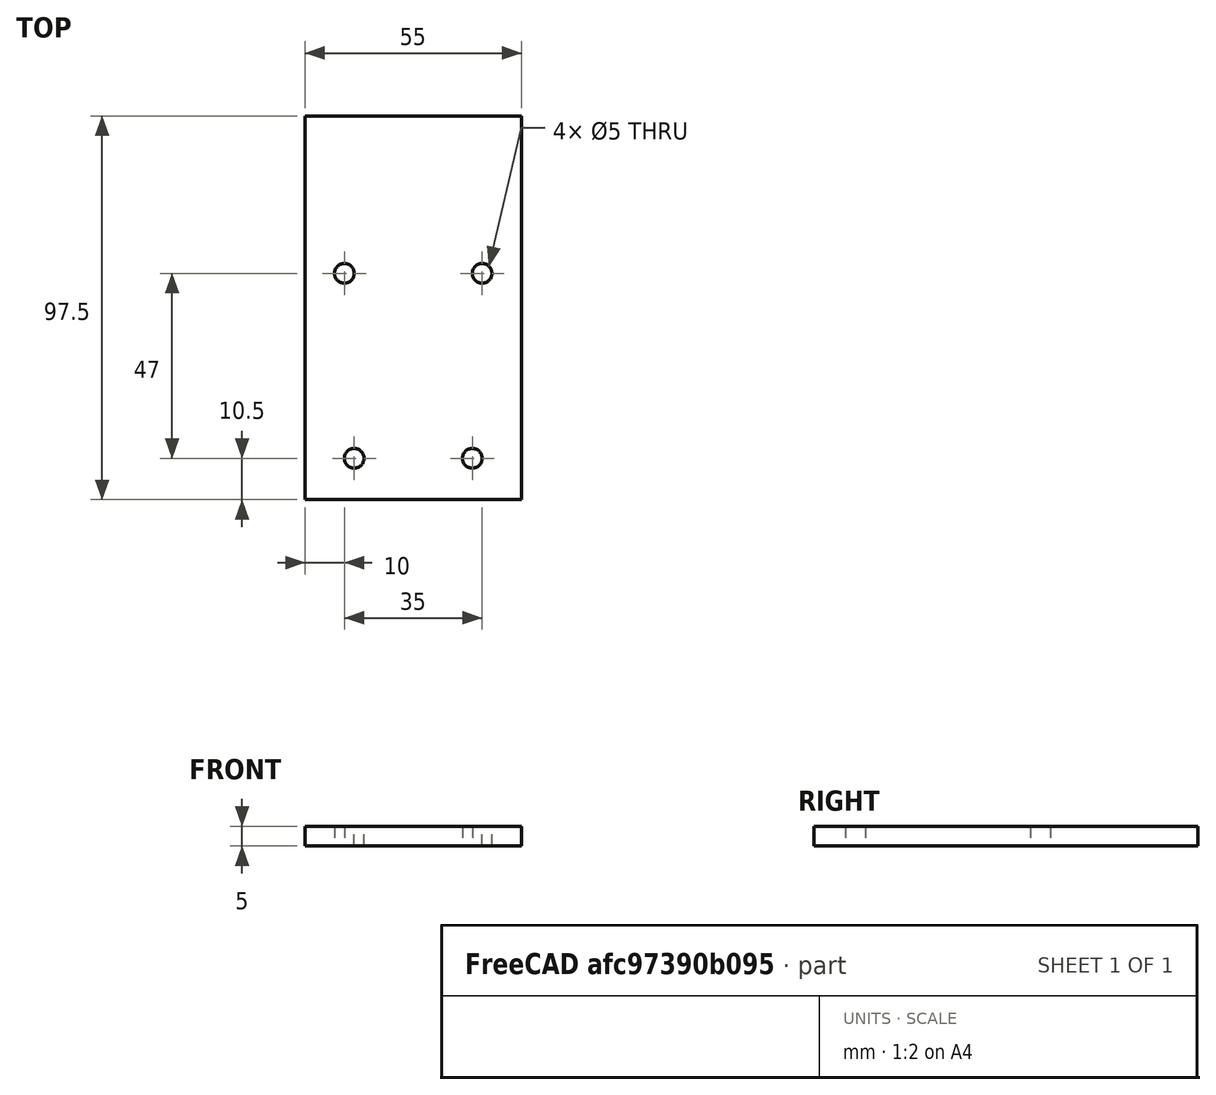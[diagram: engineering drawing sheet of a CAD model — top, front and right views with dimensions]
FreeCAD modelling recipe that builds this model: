
FCSTD DOCUMENT  (FreeCAD 0.18R15115 (Git))
Label: x axis mount plate
License: All rights reserved
LicenseURL: http://en.wikipedia.org/wiki/All_rights_reserved
objects: TechDraw::DrawProjGroupItem×3, TechDraw::DrawProjGroup×3, TechDraw::DrawViewPart×2, Sketcher::SketchObject×1, PartDesign::Pad×1, PartDesign::Body×1, TechDraw::DrawSVGTemplate×1, TechDraw::DrawPage×1
note: 4 computed .brp shape members not serialized (recipe doc carries the construction recipe); baked Part::Feature solids carry a one-line shape summary decoded from their .brp

FEATURE [Sketcher::SketchObject] Sketch
  MapMode = 5
  Support = -> [XY_Plane]
  sketch-geometry (35):
    g0: LineSegment [constr] StartX=0 StartY=0 StartZ=0 EndX=25 EndY=0 EndZ=0
    g1: LineSegment [constr] StartX=25 StartY=0 StartZ=0 EndX=25 EndY=25 EndZ=0
    g2: LineSegment [constr] StartX=25 StartY=25 StartZ=0 EndX=0 EndY=25 EndZ=0
    g3: LineSegment [constr] StartX=0 StartY=25 StartZ=0 EndX=0 EndY=0 EndZ=0
    g4: LineSegment [constr] StartX=-30 StartY=0 StartZ=0 EndX=-5 EndY=0 EndZ=0
    g5: LineSegment [constr] StartX=-5 StartY=0 StartZ=0 EndX=-5 EndY=25 EndZ=0
    g6: LineSegment [constr] StartX=-5 StartY=25 StartZ=0 EndX=-30 EndY=25 EndZ=0
    g7: LineSegment [constr] StartX=-30 StartY=25 StartZ=0 EndX=-30 EndY=0 EndZ=0
    g8: Circle CenterX=12.5 CenterY=35.5 CenterZ=0 NormalX=0 NormalY=0 NormalZ=1 AngleXU=0 Radius=2.5
    g9: Circle CenterX=-17.5 CenterY=35.5 CenterZ=0 NormalX=0 NormalY=0 NormalZ=1 AngleXU=0 Radius=2.5
    g10: LineSegment [constr] StartX=0 StartY=25 StartZ=0 EndX=12.5 EndY=35.5 EndZ=0
    g11: LineSegment [constr] StartX=12.5 StartY=35.5 StartZ=0 EndX=25 EndY=25 EndZ=0
    g12: LineSegment [constr] StartX=-5 StartY=25 StartZ=0 EndX=-17.5 EndY=35.5 EndZ=0
    g13: LineSegment [constr] StartX=-30 StartY=25 StartZ=0 EndX=-17.5 EndY=35.5 EndZ=0
    g14: LineSegment [constr] StartX=-52.5 StartY=45.5 StartZ=0 EndX=47.5 EndY=45.5 EndZ=0
    g15: LineSegment [constr] StartX=47.5 StartY=45.5 StartZ=0 EndX=47.5 EndY=70.5 EndZ=0
    g16: LineSegment [constr] StartX=47.5 StartY=70.5 StartZ=0 EndX=-52.5 EndY=70.5 EndZ=0
    g17: LineSegment [constr] StartX=-52.5 StartY=70.5 StartZ=0 EndX=-52.5 EndY=45.5 EndZ=0
    g18: LineSegment [constr] StartX=-52.5 StartY=45.5 StartZ=0 EndX=-17.5 EndY=35.5 EndZ=0
    g19: LineSegment [constr] StartX=12.5 StartY=35.5 StartZ=0 EndX=47.5 EndY=45.5 EndZ=0
    g20: Circle [constr] CenterX=15 CenterY=82.5 CenterZ=0 NormalX=0 NormalY=0 NormalZ=1 AngleXU=0 Radius=12
    g21: Circle [constr] CenterX=-20 CenterY=82.5 CenterZ=0 NormalX=0 NormalY=0 NormalZ=1 AngleXU=0 Radius=12
    g22: GeomPoint X=15 Y=70.5 Z=0
    g23: LineSegment [constr] StartX=-20 StartY=82.5 StartZ=0 EndX=-52.5 EndY=70.5 EndZ=0
    g24: LineSegment [constr] StartX=15 StartY=82.5 StartZ=0 EndX=47.5 EndY=70.5 EndZ=0
    g25: Circle CenterX=-20 CenterY=82.5 CenterZ=0 NormalX=0 NormalY=0 NormalZ=1 AngleXU=0 Radius=2.5
    g26: Circle CenterX=15 CenterY=82.5 CenterZ=0 NormalX=0 NormalY=0 NormalZ=1 AngleXU=0 Radius=2.5
    g27: LineSegment StartX=-30 StartY=122.5 StartZ=0 EndX=25 EndY=122.5 EndZ=0
    g28: LineSegment StartX=25 StartY=122.5 StartZ=0 EndX=25 EndY=25 EndZ=0
    g29: LineSegment StartX=25 StartY=25 StartZ=0 EndX=-30 EndY=25 EndZ=0
    g30: LineSegment StartX=-30 StartY=25 StartZ=0 EndX=-30 EndY=122.5 EndZ=0
    g31: LineSegment [constr] StartX=0 StartY=92.5 StartZ=0 EndX=-5 EndY=92.5 EndZ=0
    g32: LineSegment [constr] StartX=-5 StartY=92.5 StartZ=0 EndX=-5 EndY=122.5 EndZ=0
    g33: LineSegment [constr] StartX=-5 StartY=122.5 StartZ=0 EndX=0 EndY=122.5 EndZ=0
    g34: LineSegment [constr] StartX=0 StartY=122.5 StartZ=0 EndX=0 EndY=92.5 EndZ=0
  constraints (93):
    c: Coincident(g0,g1)
    c: Coincident(g1,g2)
    c: Coincident(g2,g3)
    c: Coincident(g3,g0)
    c: Horizontal(g0)
    c: Horizontal(g2)
    c: Vertical(g1)
    c: Vertical(g3)
    c: Coincident(g0,g-1)
    c: Distance(g2) = 25
    c: Distance(g1) = 25
    c: Coincident(g4,g5)
    c: Coincident(g5,g6)
    c: Coincident(g6,g7)
    c: Coincident(g7,g4)
    c: Horizontal(g4)
    c: Horizontal(g6)
    c: Vertical(g5)
    c: Vertical(g7)
    c: PointOnObject(g4,g-1)
    c: Distance(g6) = 25
    c: Distance(g5) = 25
    c: Distance(g5,g3) = 5
    c: Diameter(g8) = 5
    c: Diameter(g9) = 5
    c: Distance(g8,g2) = 10.5
    c: Distance(g9,g6) = 10.5
    c: Coincident(g10,g2)
    c: Coincident(g10,g8)
    c: Coincident(g11,g8)
    c: Coincident(g11,g1)
    c: Coincident(g12,g5)
    c: Coincident(g12,g9)
    c: Coincident(g13,g6)
    c: Coincident(g13,g9)
    c: Equal(g10,g11)
    c: Equal(g12,g13)
    c: Coincident(g14,g15)
    c: Coincident(g15,g16)
    c: Coincident(g16,g17)
    c: Coincident(g17,g14)
    c: Horizontal(g14)
    c: Horizontal(g16)
    c: Vertical(g15)
    c: Vertical(g17)
    c: Distance(g15) = 25
    c: Distance(g16) = 100
    c: Distance(g8,g14) = 10
    c: Coincident(g18,g14)
    c: Coincident(g18,g9)
    c: Coincident(g19,g8)
    c: Coincident(g19,g14)
    c: Equal(g19,g18)
    c: Diameter(g21) = 24
    c: Diameter(g20) = 24
    c: Horizontal(g20,g21)
    c: PointOnObject(g22,g20)
    c: Vertical(g22,g20)
    c: PointOnObject(g22,g16)
    c: Coincident(g23,g16)
    c: Coincident(g24,g20)
    c: Coincident(g24,g15)
    c: Equal(g24,g23)
    c: Coincident(g23,g21)
    c: Distance(g21,g20) = 35
    c: Coincident(g25,g21)
    c: Coincident(g26,g20)
    c: Diameter(g26) = 5
    c: Diameter(g25) = 5
    c: Coincident(g27,g28)
    c: Coincident(g28,g29)
    c: Coincident(g29,g30)
    c: Coincident(g30,g27)
    c: Horizontal(g27)
    c: Horizontal(g29)
    c: Vertical(g28)
    c: Vertical(g30)
    c: PointOnObject(g1,g29)
    c: Distance(g26,g28) = 10
    c: Distance(g25,g30) = 10
    c: Coincident(g31,g32)
    c: Coincident(g32,g33)
    c: Coincident(g33,g34)
    c: Coincident(g34,g31)
    c: Horizontal(g31)
    c: Horizontal(g33)
    c: Vertical(g32)
    c: Vertical(g34)
    c: PointOnObject(g31,g-2)
    c: Distance(g33) = 5
    c: Distance(g32) = 30
    c: DistanceY(g25,g31) = 10
    c: PointOnObject(g33,g27)
FEATURE [PartDesign::Pad] Pad
  Length = 5
  Length2 = 100
  Profile = -> Sketch
  Type = 0
FEATURE [PartDesign::Body] Body
  Group = -> [Sketch,Pad]
  Origin = -> Origin
  Tip = -> Pad
FEATURE [TechDraw::DrawSVGTemplate] Template
  EditableTexts = Approved1=Approved 1; Approved2=Approved 2; CheckedBy=Checked By; Code=Code; CompanyAddress=1234 Main St; CompanyName=Company Name; DrawingNumber=Drawing Number; DrawingTitle1=Drawing Title 1; DrawingTitle2=Drawing Title 2; DrawingTitle3=Drawing Title 3; DrawnBy=Drawn By; Revision=Rev; Scale=Scale; Sheet=Sheet n of m; Weight=Weight
  Height = 215.9
  Orientation = 1
  Width = 279.4
FEATURE [TechDraw::DrawProjGroupItem] ProjItem  label="Front"
  CoarseView = false
  Direction = (0,0,1)
  Focus = 100
  HardHidden = false
  IsoCount = 0
  IsoHidden = false
  IsoVisible = false
  LockPosition = false
  Perspective = false
  Rotation = 0
  RotationVector = (1,0,0)
  ScaleType = 2
  SeamHidden = false
  SeamVisible = false
  SmoothHidden = false
  SmoothVisible = false
  Source = -> [Body]
  Type = 0
  X = 0
  Y = 0
FEATURE [TechDraw::DrawProjGroup] ProjGroup
  Anchor = -> ProjItem
  AutoDistribute = true
  LockPosition = false
  ProjectionType = 0
  Rotation = 0
  ScaleType = 0
  Source = -> [Body]
  Views = -> [ProjItem]
  X = 59.0685
  Y = 163.51
  spacingX = 15
  spacingY = 15
FEATURE [TechDraw::DrawViewPart] View
  CoarseView = false
  Direction = (0,0,1)
  Focus = 100
  HardHidden = false
  IsoCount = 0
  IsoHidden = false
  IsoVisible = false
  LockPosition = false
  Perspective = false
  Rotation = 0
  ScaleType = 0
  SeamHidden = false
  SeamVisible = false
  SmoothHidden = false
  SmoothVisible = false
  Source = -> [Body]
  X = 139.7
  Y = 107.95
FEATURE [TechDraw::DrawProjGroupItem] ProjItem001  label="Front001"
  CoarseView = false
  Direction = (0,0,1)
  Focus = 100
  HardHidden = false
  IsoCount = 0
  IsoHidden = false
  IsoVisible = false
  LockPosition = false
  Perspective = false
  Rotation = 0
  RotationVector = (1,0,0)
  ScaleType = 2
  SeamHidden = false
  SeamVisible = false
  SmoothHidden = false
  SmoothVisible = false
  Source = -> [Body]
  Type = 0
  X = 0
  Y = 0
FEATURE [TechDraw::DrawProjGroup] ProjGroup001
  Anchor = -> ProjItem001
  AutoDistribute = true
  LockPosition = false
  ProjectionType = 0
  Rotation = 0
  ScaleType = 0
  Source = -> [Body]
  Views = -> [ProjItem001]
  X = 207.871
  Y = 145.265
  spacingX = 15
  spacingY = 15
FEATURE [TechDraw::DrawViewPart] View001
  CoarseView = false
  Direction = (0,0,1)
  Focus = 100
  HardHidden = false
  IsoCount = 0
  IsoHidden = false
  IsoVisible = false
  LockPosition = false
  Perspective = false
  Rotation = 0
  ScaleType = 0
  SeamHidden = false
  SeamVisible = false
  SmoothHidden = false
  SmoothVisible = false
  Source = -> [Body]
  X = 139.7
  Y = 107.95
FEATURE [TechDraw::DrawProjGroupItem] ProjItem002  label="Front002"
  CoarseView = false
  Direction = (0,0,1)
  Focus = 100
  HardHidden = false
  IsoCount = 0
  IsoHidden = false
  IsoVisible = false
  LockPosition = false
  Perspective = false
  Rotation = 0
  RotationVector = (1,0,0)
  ScaleType = 2
  SeamHidden = false
  SeamVisible = false
  SmoothHidden = false
  SmoothVisible = false
  Source = -> [Body]
  Type = 0
  X = 0
  Y = 0
FEATURE [TechDraw::DrawProjGroup] ProjGroup002
  Anchor = -> ProjItem002
  AutoDistribute = true
  LockPosition = false
  ProjectionType = 0
  Rotation = 0
  ScaleType = 0
  Source = -> [Body]
  Views = -> [ProjItem002]
  X = 58.7177
  Y = 60.8158
  spacingX = 15
  spacingY = 15
FEATURE [TechDraw::DrawPage] Page
  KeepUpdated = true
  ProjectionType = 0
  Template = -> Template
  Views = -> [ProjGroup,View,ProjGroup001,View001,ProjGroup002]
